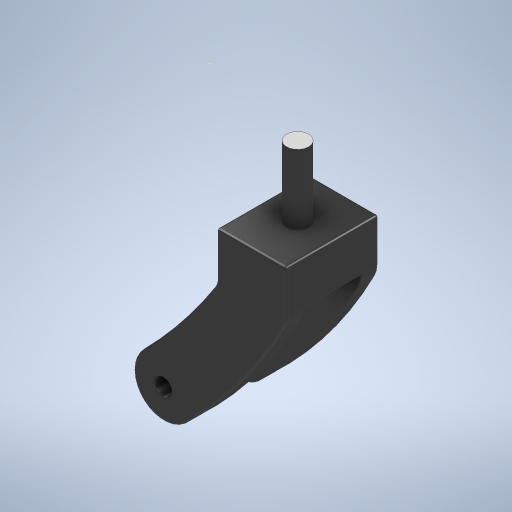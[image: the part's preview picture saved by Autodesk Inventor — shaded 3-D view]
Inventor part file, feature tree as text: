
AUTODESK INVENTOR PART (.ipt)
format: ipt  version: 2023 (Build 270158000, 158)  size: 380,416 bytes
history: native  units: in
note: dims shown in document units (in); Inventor stores cm internally (conversion verified against a paired STEP export)
features: fillet x8, sketch x7, extrude x4, other x1
ambient origin geometry x8: Origin, YZ Plane, XZ Plane, XY Plane, X Axis, Y Axis, Z Axis, Center Point
bodies: Solid1 (feature_tree)
feature tree (20):
  sketch  "Sketch1"  dims[d2=1.0236in d3=0.5906in d6=2.3622in d8=2.9921in]
  sketch  "Sketch2"  dims[d10=0.0in d11=3.937in]
  other  "Work Point1"
  sketch  "Sketch3"  dims[d12=1.6535in d13=3.1496in d14=0.0in d15=0.7874in d16=0.5906in d17=0.5906in d18=0.5906in d19=0.3937in d20=0.0in d21=0.75in]
  extrude  "Extrusion1"  Depth=0.5906in
  fillet  "Fillet1"  Radius=2.3622in
  fillet  "Fillet2"  Radius=2.9921in
  extrude  "Extrusion2"  Depth=3.937in
  extrude  "Extrusion3"  Depth=0.3937in TaperAngle=0.0deg
  fillet  "Fillet3"  Radius=0.7874in
  fillet  "Fillet4"  Radius=0.5906in
  fillet  "Fillet5"  Radius=0.5906in
  fillet  "Fillet6"  Radius=0.5906in
  fillet  "Fillet7"  Radius=0.3937in
  fillet  "Fillet8"  Radius=0.75in
  sketch  "Sketch6"  dims[d26=0.0787in]
  extrude  "Extrusion4"  Depth=0.0787in
  sketch  "Sketch4"  dims[d22=3.1496in d23=0.0in d24=0.0787in]
  sketch  "Sketch5"  dims[d25=0.0787in]
  sketch  "Sketch7"  dims[d27=0.0787in d28=0.0787in d29=0.0787in d30=0.7677in d31=0.0in d32=0.0in d33=0.0in d34=0.0197in d35=0.0344in]
